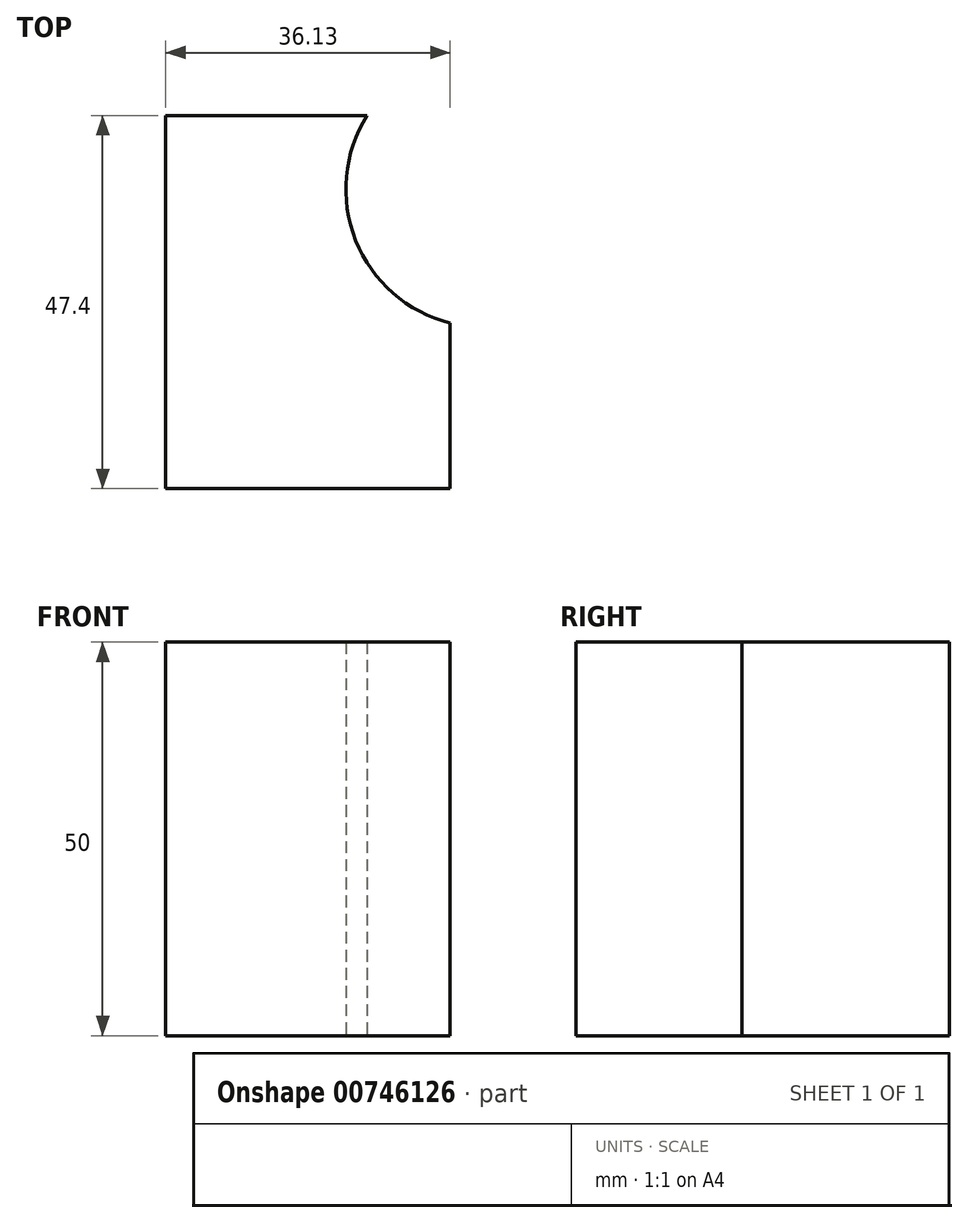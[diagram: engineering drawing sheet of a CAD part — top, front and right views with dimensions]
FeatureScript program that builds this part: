
annotation { "Feature Type Name" : "Feature", "Feature Type Description" : "" }
export const myFeature = defineFeature(function(context is Context, id is Id, definition is map)
    precondition{}
    {
        {
            var Q0;
            Q0=qCreatedBy(makeId("Top.planeOp"),FACE);
            var sketch = newSketch(context, id + "F0", { "sketchPlane" : qUnion([Q0])});
            skLineSegment(sketch, "E0.bottom", {"start": v(-64.18, 0) * mm, "end": v(-28.05, 0) * mm});
            skLineSegment(sketch, "E0.top", {"start": v(-64.18, -47.4) * mm, "end": v(-28.05, -47.4) * mm});
            skLineSegment(sketch, "E0.left", {"start": v(-64.18, 0) * mm, "end": v(-64.18, -47.4) * mm});
            skLineSegment(sketch, "E0.right", {"start": v(-28.05, 0) * mm, "end": v(-28.05, -47.4) * mm});
            skSolve(sketch);
        }
        {
            var Q0;
            Q0=makeQuery(id+"F0.imprint","IMPRINT",FACE,{"disambiguationData":[TD([[makeQuery(id+"F0.imprint","IMPRINT",EDGE,{"derivedFrom":sQuery(id+"F0.wireOp",EDGE,"E0.bottom")}),-1.0]])]});
            extrude(context, id + "F1", {"entities" : qUnion([Q0]), "depth" : 50 * mm, "offsetDistance" : 25.4 * mm});
        }
        {
            var Q0;
            Q0=qCreatedBy(makeId("Top.planeOp"),FACE);
            var sketch = newSketch(context, id + "F2", { "sketchPlane" : qUnion([Q0])});
            skSolve(sketch);
        }
        {
            var Q0;
            Q0=qCreatedBy(makeId("Top.planeOp"),FACE);
            var sketch = newSketch(context, id + "F3", { "sketchPlane" : qUnion([Q0])});
            skCircle(sketch, "E1", {"center": v(-23.78, -9.38) * mm, "radius": 17.52 * mm});
            skSolve(sketch);
        }
        {
            var Q0;
            Q0=makeQuery(id+"F3.imprint","IMPRINT",FACE,{"disambiguationData":[TD([[makeQuery(id+"F3.imprint","IMPRINT",EDGE,{"derivedFrom":sQuery(id+"F3.wireOp",EDGE,"E1")}),1.0]])]});
            var Q1;
            Q1 = qSketchRegion(id + "F2", true);
            extrude(context, id + "F4", {"entities" : qUnion([Q0, Q1]), "operationType" : NewBodyOperationType.REMOVE, "depth" : 50 * mm, "offsetDistance" : 25 * mm});
        }
    });
